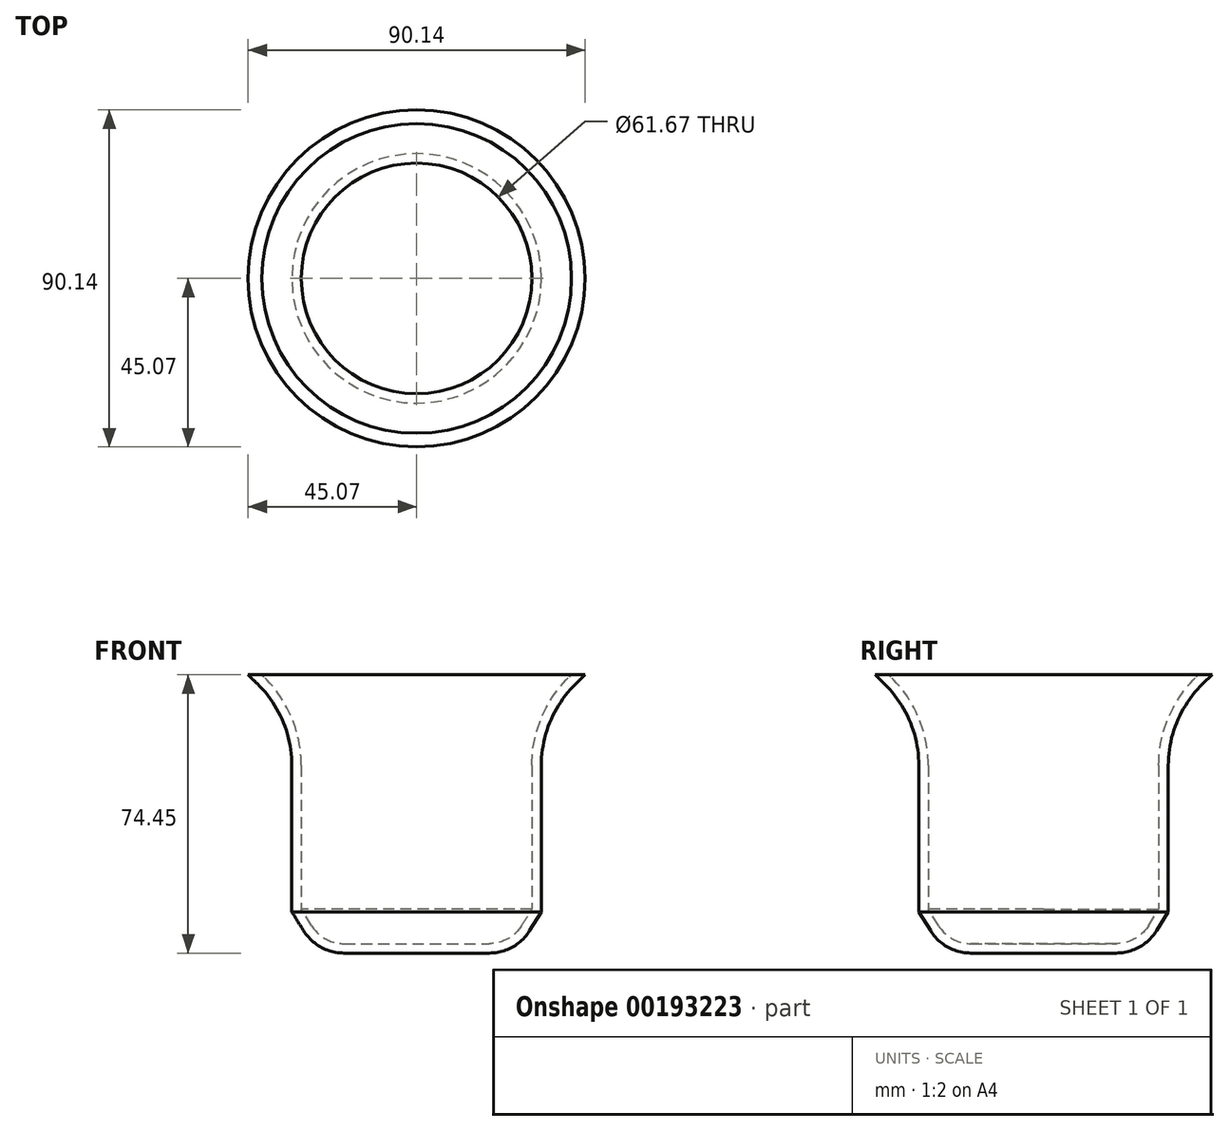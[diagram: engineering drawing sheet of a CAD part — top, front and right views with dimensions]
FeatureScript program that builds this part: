
annotation { "Feature Type Name" : "Feature", "Feature Type Description" : "" }
export const myFeature = defineFeature(function(context is Context, id is Id, definition is map)
    precondition{}
    {
        {
            var Q0;
            Q0=qCreatedBy(makeId("Front.planeOp"),FACE);
            var sketch = newSketch(context, id + "F0", { "sketchPlane" : qUnion([Q0])});
            skLineSegment(sketch, "E0", {"start": v(0, 35.51) * mm, "end": v(45.07, 35.51) * mm});
            skLineSegment(sketch, "E1", {"start": v(45.07, 35.51) * mm, "end": v(42.62, 33.13) * mm});
            skLineSegment(sketch, "E2", {"start": v(33.37, 11.27) * mm, "end": v(33.37, -27.9) * mm});
            skLineSegment(sketch, "E3", {"start": v(33.37, -27.9) * mm, "end": v(30.24, -32.95) * mm});
            skLineSegment(sketch, "E4", {"start": v(19.45, -38.94) * mm, "end": v(0, -38.94) * mm});
            skLineSegment(sketch, "E5", {"start": v(0, -38.94) * mm, "end": v(0, 35.51) * mm});
            skPoint(sketch, "E6.visualSharp", {"position": v(33.37, 24.15) * mm});
            skArc(sketch, "E6.filletArc", {"start": v(42.62, 33.13) * mm, "mid": v(35.78, 23.14) * mm, "end": v(33.37, 11.27) * mm});
            skPoint(sketch, "E7.visualSharp", {"position": v(26.5, -38.94) * mm});
            skArc(sketch, "E7.filletArc", {"start": v(19.45, -38.94) * mm, "mid": v(25.62, -37.34) * mm, "end": v(30.24, -32.95) * mm});
            skSolve(sketch);
        }
        {
            var Q0;
            Q0=makeQuery(id+"F0.imprint","IMPRINT",FACE,{"disambiguationData":[TD([[makeQuery(id+"F0.imprint","IMPRINT",EDGE,{"derivedFrom":sQuery(id+"F0.wireOp",EDGE,"E0")}),-1.0]])]});
            var Q1;
            Q1=sQuery(id+"F0.wireOp",EDGE,"E5");
            revolve(context, id + "F1", {"entities" : qUnion([Q0]), "axis" : qUnion([Q1]), "revolveType" : RevolveType.FULL});
        }
        {
            var Q0;
            Q0=makeQuery(id+"F1.opRevolve","SWEPT_FACE",FACE,{"disambiguationData":[OSD([sQuery(id+"F0.wireOp",EDGE,"E0")])]});
            shell(context, id + "F2", {"entities" : qUnion([Q0]), "thickness" : 2.54 * mm});
        }
    });
